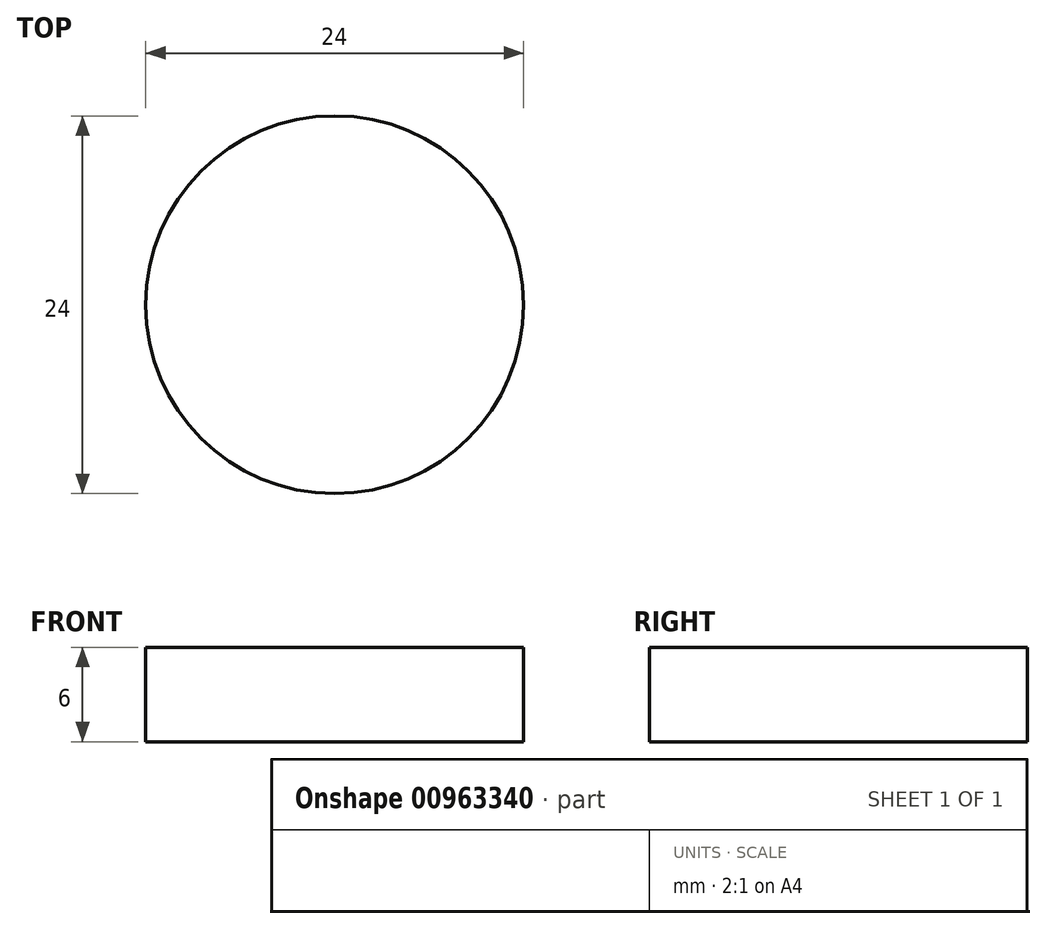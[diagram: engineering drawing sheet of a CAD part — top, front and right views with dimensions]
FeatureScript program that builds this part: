
annotation { "Feature Type Name" : "Feature", "Feature Type Description" : "" }
export const myFeature = defineFeature(function(context is Context, id is Id, definition is map)
    precondition{}
    {
        {
            var Q0;
            Q0=qCreatedBy(makeId("Top.planeOp"),FACE);
            var sketch = newSketch(context, id + "F0", { "sketchPlane" : qUnion([Q0])});
            skCircle(sketch, "E0", {"center": v(0, 0) * mm, "radius": 12 * mm});
            skSolve(sketch);
        }
        {
            var Q0;
            Q0 = qSketchRegion(id + "F0", true);
            var Q1;
            Q1=makeQuery(id+"F0.imprint","IMPRINT",FACE,{"disambiguationData":[TD([[makeQuery(id+"F0.imprint","IMPRINT",EDGE,{"derivedFrom":sQuery(id+"F0.wireOp",EDGE,"E0")}),1.0]])]});
            extrude(context, id + "F1", {"entities" : qUnion([Q0, Q1]), "depth" : 6 * mm, "offsetDistance" : 25 * mm});
        }
    });
